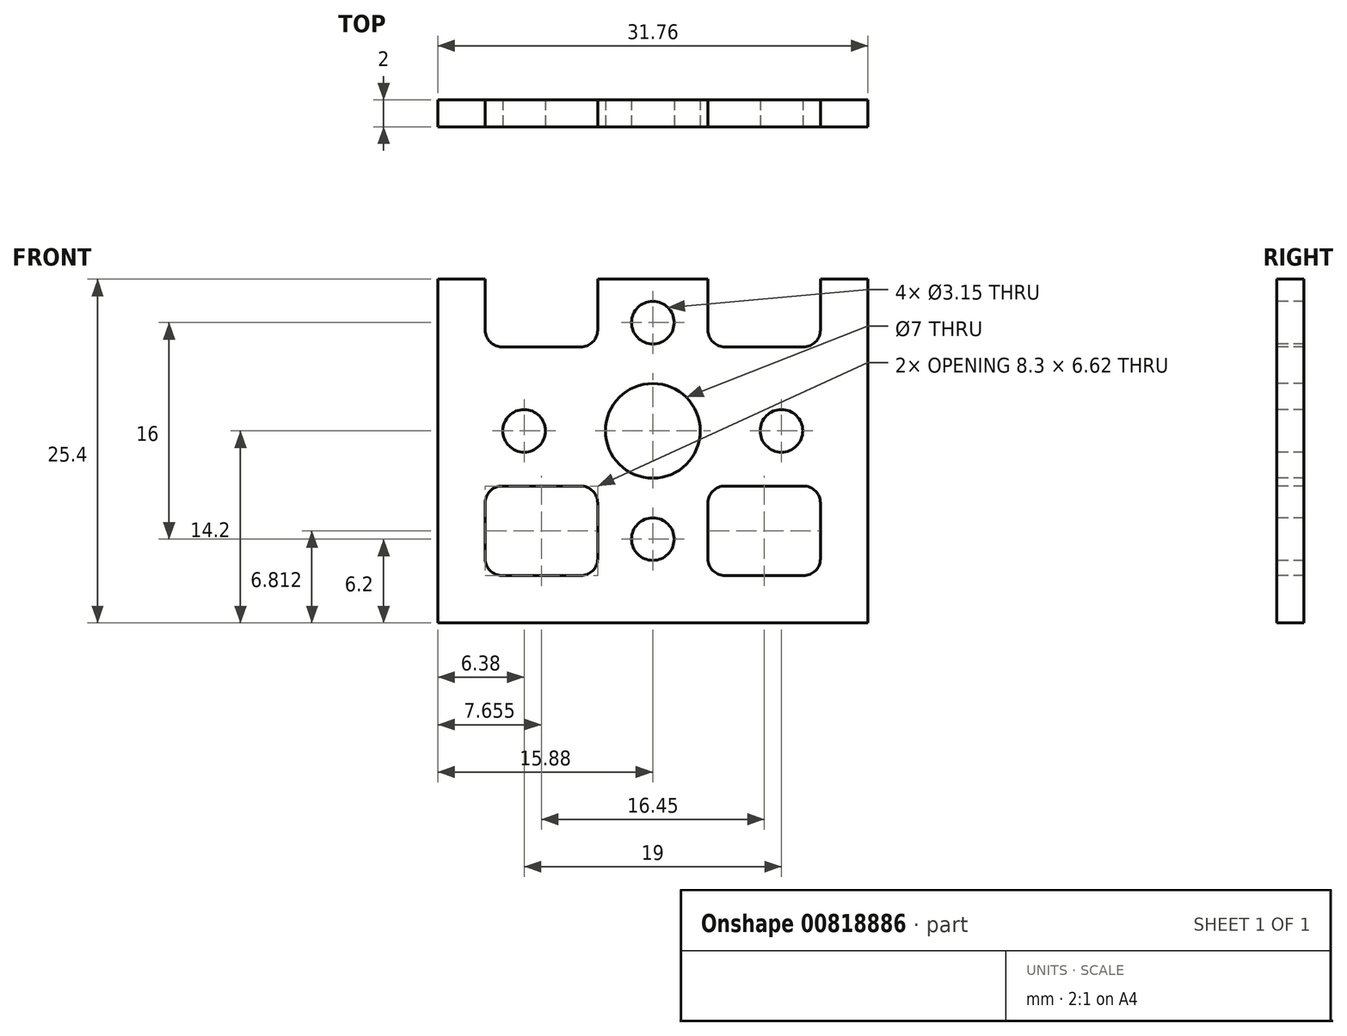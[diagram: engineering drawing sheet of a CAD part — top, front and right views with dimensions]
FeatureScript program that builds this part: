
annotation { "Feature Type Name" : "Feature", "Feature Type Description" : "" }
export const myFeature = defineFeature(function(context is Context, id is Id, definition is map)
    precondition{}
    {
        {
            assignVariable(context, id + "F0", {"name" : "firewall_thickness_mm", "anyValue" : 2});
        }
        {
            var Q0;
            Q0=qCreatedBy(makeId("Front.planeOp"),FACE);
            var sketch = newSketch(context, id + "F1", { "sketchPlane" : qUnion([Q0])});
            skLineSegment(sketch, "E0.bottom", {"start": v(15.88, 12.7) * mm, "end": v(-15.88, 12.7) * mm});
            skLineSegment(sketch, "E0.top", {"start": v(15.88, -12.7) * mm, "end": v(-15.88, -12.7) * mm});
            skLineSegment(sketch, "E0.left", {"start": v(15.88, 12.7) * mm, "end": v(15.87, -12.7) * mm});
            skLineSegment(sketch, "E0.right", {"start": v(-15.88, 12.7) * mm, "end": v(-15.88, -12.7) * mm});
            skPoint(sketch, "E0.middle", {"position": v(0, 0) * mm});
            skSolve(sketch);
        }
        {
            var Q0;
            Q0 = qSketchRegion(id + "F1", true);
            extrude(context, id + "F2", {"entities" : qUnion([Q0]), "oppositeDirection" : true, "depth" : (getVariable(context, 'firewall_thickness_mm')) * mm, "offsetDistance" : 25 * mm});
        }
        {
            var Q0;
            Q0=makeQuery(id+"F1.imprint","IMPRINT",FACE,{"disambiguationData":[TD([[makeQuery(id+"F1.imprint","IMPRINT",EDGE,{"derivedFrom":sQuery(id+"F1.wireOp",EDGE,"E0.bottom")}),1.0]])]});
            var sketch = newSketch(context, id + "F3", { "sketchPlane" : qUnion([Q0])});
            skCircle(sketch, "E1", {"center": v(0, 1.5) * mm, "radius": 3.5 * mm});
            skCircle(sketch, "E2", {"center": v(-9.5, 1.5) * mm, "radius": 1.57 * mm});
            skCircle(sketch, "E3.MirrorC", {"center": v(9.5, 1.5) * mm, "radius": 1.57 * mm});
            skCircle(sketch, "E4", {"center": v(0, 9.5) * mm, "radius": 1.57 * mm});
            skLineSegment(sketch, "E5", {"start": v(-15.88, 1.5) * mm, "end": v(15.88, 1.5) * mm, "construction": true});
            skLineSegment(sketch, "E6", {"start": v(0, 12.7) * mm, "end": v(0, -12.7) * mm, "construction": true});
            skCircle(sketch, "E7.MirrorC", {"center": v(0, -6.5) * mm, "radius": 1.57 * mm});
            skSolve(sketch);
        }
        {
            var Q0;
            Q0=makeQuery(id+"F1.imprint","IMPRINT",FACE,{"disambiguationData":[TD([[makeQuery(id+"F1.imprint","IMPRINT",EDGE,{"derivedFrom":sQuery(id+"F1.wireOp",EDGE,"E0.bottom")}),1.0]])]});
            var sketch = newSketch(context, id + "F4", { "sketchPlane" : qUnion([Q0])});
            skLineSegment(sketch, "E8.bottom", {"start": v(-14.88, -0.07) * mm, "end": v(-1.57, -0.07) * mm, "construction": true});
            skLineSegment(sketch, "E8.top", {"start": v(-14.88, -11.7) * mm, "end": v(-1.57, -11.7) * mm, "construction": true});
            skLineSegment(sketch, "E8.left", {"start": v(-14.88, -0.08) * mm, "end": v(-14.88, -11.7) * mm, "construction": true});
            skLineSegment(sketch, "E8.right", {"start": v(-1.58, -0.08) * mm, "end": v(-1.57, -11.7) * mm, "construction": true});
            skLineSegment(sketch, "E9.0", {"start": v(-4.08, -3.83) * mm, "end": v(-4.08, -7.95) * mm});
            skLineSegment(sketch, "E9.1", {"start": v(-11.13, -2.58) * mm, "end": v(-5.33, -2.58) * mm});
            skLineSegment(sketch, "E9.2", {"start": v(-12.38, -3.83) * mm, "end": v(-12.38, -7.95) * mm});
            skLineSegment(sketch, "E9.3", {"start": v(-11.13, -9.2) * mm, "end": v(-5.33, -9.2) * mm});
            skPoint(sketch, "E10.visualSharp", {"position": v(-12.38, -2.58) * mm});
            skArc(sketch, "E10.filletArc", {"start": v(-11.13, -2.58) * mm, "mid": v(-12, -2.94) * mm, "end": v(-12.38, -3.83) * mm});
            skPoint(sketch, "E11.visualSharp", {"position": v(-4.07, -2.58) * mm});
            skArc(sketch, "E11.filletArc", {"start": v(-4.07, -3.83) * mm, "mid": v(-4.44, -2.94) * mm, "end": v(-5.33, -2.58) * mm});
            skPoint(sketch, "E12.visualSharp", {"position": v(-4.07, -9.2) * mm});
            skArc(sketch, "E12.filletArc", {"start": v(-5.33, -9.2) * mm, "mid": v(-4.44, -8.83) * mm, "end": v(-4.07, -7.95) * mm});
            skPoint(sketch, "E13.visualSharp", {"position": v(-12.38, -9.2) * mm});
            skArc(sketch, "E13.filletArc", {"start": v(-12.38, -7.95) * mm, "mid": v(-12, -8.83) * mm, "end": v(-11.13, -9.2) * mm});
            skArc(sketch, "E14.MirrorCS", {"start": v(4.07, -3.83) * mm, "mid": v(4.44, -2.94) * mm, "end": v(5.33, -2.58) * mm});
            skLineSegment(sketch, "E15.MirrorCS", {"start": v(11.13, -2.58) * mm, "end": v(5.33, -2.58) * mm});
            skArc(sketch, "E16.MirrorCS", {"start": v(11.13, -2.58) * mm, "mid": v(12, -2.94) * mm, "end": v(12.38, -3.83) * mm});
            skLineSegment(sketch, "E17.MirrorCS", {"start": v(12.38, -3.83) * mm, "end": v(12.38, -7.95) * mm});
            skArc(sketch, "E18.MirrorCS", {"start": v(12.38, -7.95) * mm, "mid": v(12, -8.83) * mm, "end": v(11.13, -9.2) * mm});
            skLineSegment(sketch, "E19.MirrorCS", {"start": v(11.13, -9.2) * mm, "end": v(5.33, -9.2) * mm});
            skArc(sketch, "E20.MirrorCS", {"start": v(5.33, -9.2) * mm, "mid": v(4.44, -8.83) * mm, "end": v(4.07, -7.95) * mm});
            skLineSegment(sketch, "E21.MirrorCS", {"start": v(4.08, -3.83) * mm, "end": v(4.08, -7.95) * mm});
            skLineSegment(sketch, "E22", {"start": v(-12.38, 12.7) * mm, "end": v(-12.38, 8.95) * mm});
            skLineSegment(sketch, "E23", {"start": v(-4.08, 8.95) * mm, "end": v(-4.08, 12.7) * mm});
            skLineSegment(sketch, "E24", {"start": v(-11.13, 7.7) * mm, "end": v(-5.33, 7.7) * mm});
            skPoint(sketch, "E25.visualSharp", {"position": v(-12.38, 7.7) * mm});
            skArc(sketch, "E25.filletArc", {"start": v(-12.38, 8.95) * mm, "mid": v(-12, 8.07) * mm, "end": v(-11.13, 7.7) * mm});
            skPoint(sketch, "E26.visualSharp", {"position": v(-4.08, 7.7) * mm});
            skArc(sketch, "E26.filletArc", {"start": v(-5.33, 7.7) * mm, "mid": v(-4.44, 8.07) * mm, "end": v(-4.08, 8.95) * mm});
            skLineSegment(sketch, "E27.MirrorCS", {"start": v(4.08, 8.95) * mm, "end": v(4.07, 12.7) * mm});
            skArc(sketch, "E28.MirrorCS", {"start": v(5.33, 7.7) * mm, "mid": v(4.44, 8.07) * mm, "end": v(4.08, 8.95) * mm});
            skLineSegment(sketch, "E29.MirrorCS", {"start": v(11.13, 7.7) * mm, "end": v(5.33, 7.7) * mm});
            skArc(sketch, "E30.MirrorCS", {"start": v(12.38, 8.95) * mm, "mid": v(12, 8.07) * mm, "end": v(11.13, 7.7) * mm});
            skLineSegment(sketch, "E31.MirrorCS", {"start": v(12.38, 12.7) * mm, "end": v(12.38, 8.95) * mm});
            skLineSegment(sketch, "E32", {"start": v(-12.38, 12.7) * mm, "end": v(-4.08, 12.7) * mm});
            skLineSegment(sketch, "E33.MirrorCS", {"start": v(12.38, 12.7) * mm, "end": v(4.08, 12.7) * mm});
            skLineSegment(sketch, "E34.0", {"start": v(-15.88, -12.7) * mm, "end": v(0, -12.7) * mm});
            skLineSegment(sketch, "E34.1", {"start": v(-15.88, 0) * mm, "end": v(-15.88, -12.7) * mm});
            skSolve(sketch);
        }
        {
            var Q0;
            Q0 = qSketchRegion(id + "F3", true);
            var Q1;
            Q1 = qSketchRegion(id + "F4", true);
            extrude(context, id + "F5", {"entities" : qUnion([Q0, Q1]), "operationType" : NewBodyOperationType.REMOVE, "endBound" : BoundingType.THROUGH_ALL, "oppositeDirection" : true, "depth" : 25 * mm, "offsetDistance" : 25 * mm});
        }
    });
